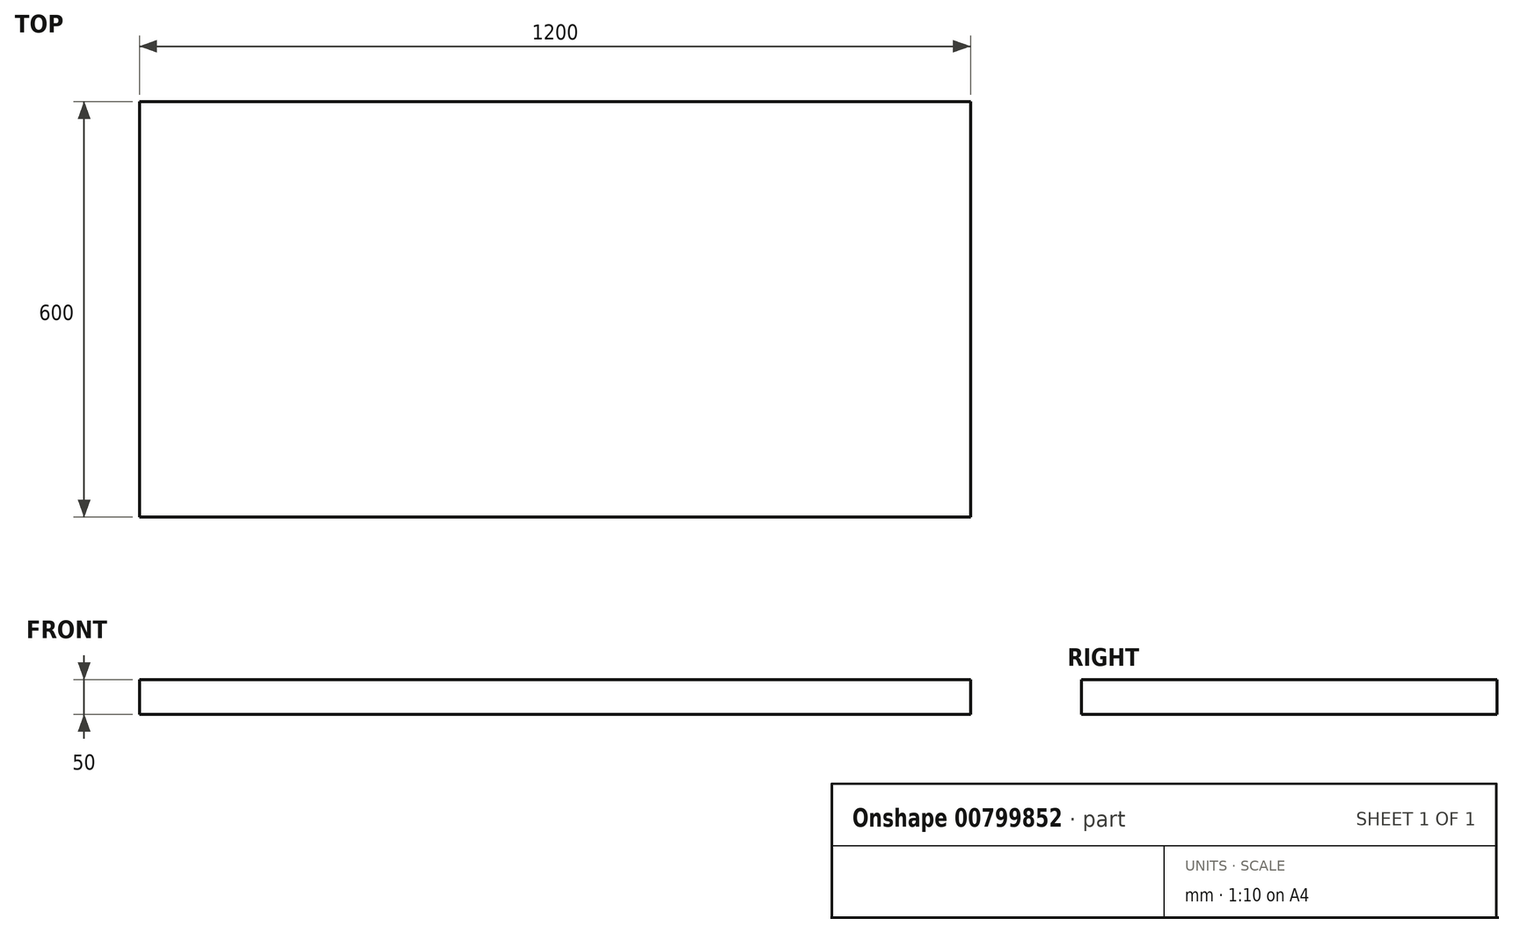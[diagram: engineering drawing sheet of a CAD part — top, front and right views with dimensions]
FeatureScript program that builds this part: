
annotation { "Feature Type Name" : "Feature", "Feature Type Description" : "" }
export const myFeature = defineFeature(function(context is Context, id is Id, definition is map)
    precondition{}
    {
        {
            var Q0;
            Q0=qCreatedBy(makeId("Top.planeOp"),FACE);
            var sketch = newSketch(context, id + "F0", { "sketchPlane" : qUnion([Q0])});
            skLineSegment(sketch, "E0.bottom", {"start": v(600, -300) * mm, "end": v(-600, -300) * mm});
            skLineSegment(sketch, "E0.top", {"start": v(600, 300) * mm, "end": v(-600, 300) * mm});
            skLineSegment(sketch, "E0.left", {"start": v(600, -300) * mm, "end": v(600, 300) * mm});
            skLineSegment(sketch, "E0.right", {"start": v(-600, -300) * mm, "end": v(-600, 300) * mm});
            skPoint(sketch, "E0.middle", {"position": v(0, 0) * mm});
            skSolve(sketch);
        }
        {
            var Q0;
            Q0=makeQuery(id+"F0.imprint","IMPRINT",FACE,{"disambiguationData":[TD([[makeQuery(id+"F0.imprint","IMPRINT",EDGE,{"derivedFrom":sQuery(id+"F0.wireOp",EDGE,"E0.bottom")}),-1.0]])]});
            extrude(context, id + "F1", {"entities" : qUnion([Q0]), "depth" : 50 * mm, "offsetDistance" : 25 * mm});
        }
    });
